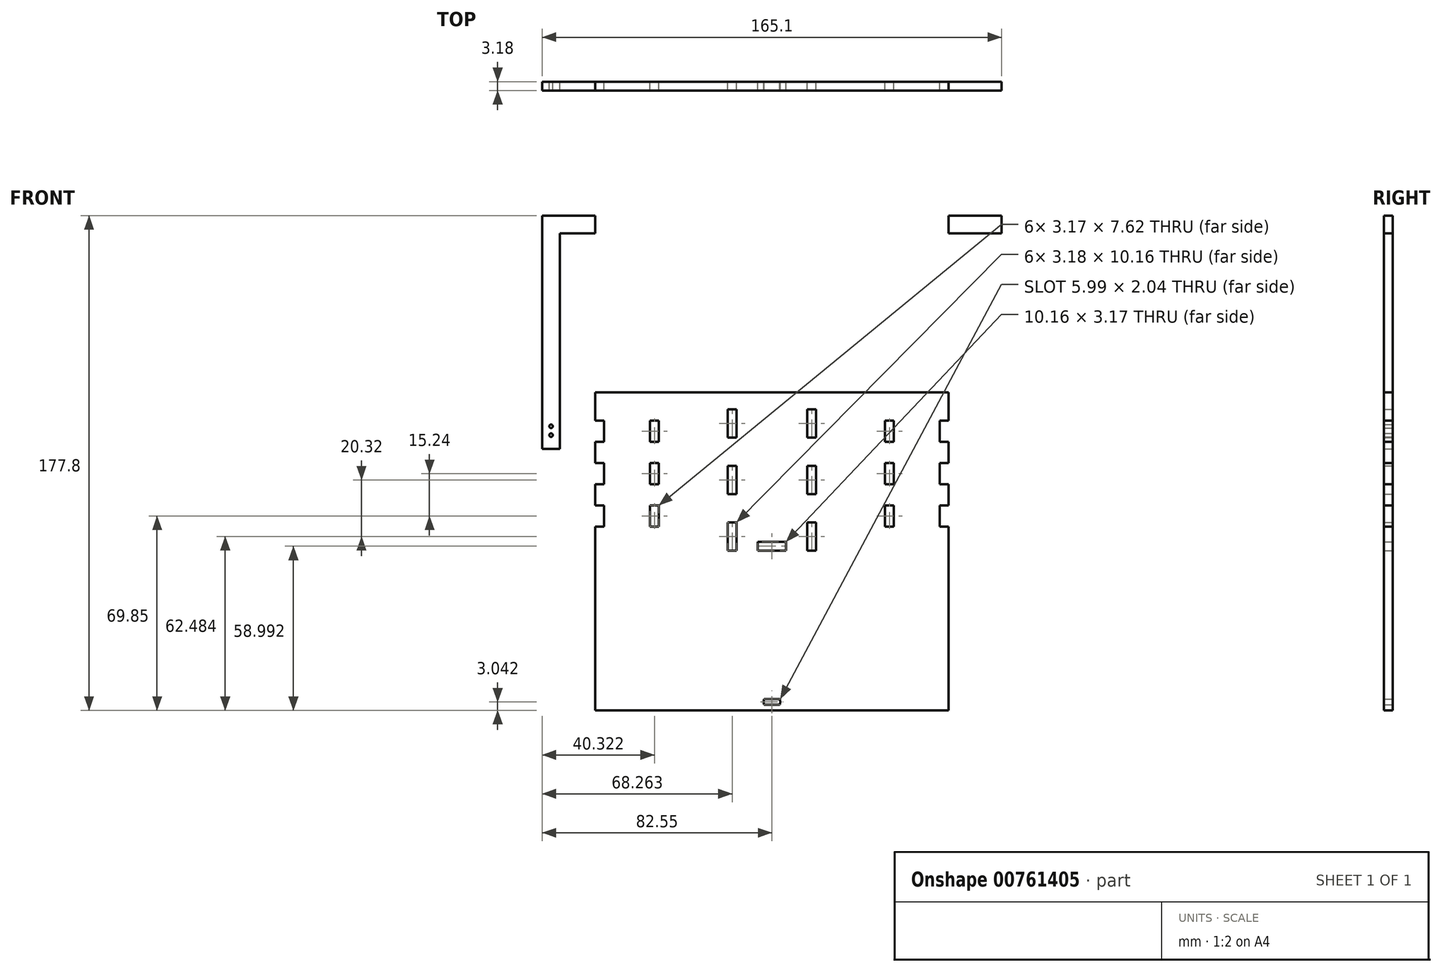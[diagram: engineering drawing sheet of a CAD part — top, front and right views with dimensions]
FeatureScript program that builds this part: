
annotation { "Feature Type Name" : "Feature", "Feature Type Description" : "" }
export const myFeature = defineFeature(function(context is Context, id is Id, definition is map)
    precondition{}
    {
        {
            var Q0;
            Q0=qCreatedBy(makeId("Front.planeOp"),FACE);
            var sketch = newSketch(context, id + "F0", { "sketchPlane" : qUnion([Q0])});
            skLineSegment(sketch, "E0.top", {"start": v(63.5, 57.15) * mm, "end": v(-63.5, 57.15) * mm});
            skPoint(sketch, "E0.middle", {"position": v(0, 0) * mm});
            skLineSegment(sketch, "E1.bottom", {"start": v(-63.5, 16.5) * mm, "end": v(-60.33, 16.5) * mm});
            skLineSegment(sketch, "E1.top", {"start": v(-63.5, 8.89) * mm, "end": v(-60.33, 8.89) * mm});
            skLineSegment(sketch, "E1.left", {"start": v(-63.5, 16.5) * mm, "end": v(-63.5, 8.89) * mm});
            skLineSegment(sketch, "E1.right", {"start": v(-60.33, 16.5) * mm, "end": v(-60.33, 8.89) * mm});
            skLineSegment(sketch, "E2.bottom", {"start": v(-43.82, 16.5) * mm, "end": v(-40.64, 16.5) * mm});
            skLineSegment(sketch, "E2.top", {"start": v(-43.82, 8.89) * mm, "end": v(-40.64, 8.89) * mm});
            skLineSegment(sketch, "E2.left", {"start": v(-43.82, 16.5) * mm, "end": v(-43.82, 8.89) * mm});
            skLineSegment(sketch, "E2.right", {"start": v(-40.64, 16.5) * mm, "end": v(-40.64, 8.89) * mm});
            skLineSegment(sketch, "E3.bottom", {"start": v(-40.64, 31.75) * mm, "end": v(-43.82, 31.75) * mm});
            skLineSegment(sketch, "E3.top", {"start": v(-40.64, 24.13) * mm, "end": v(-43.82, 24.13) * mm});
            skLineSegment(sketch, "E3.left", {"start": v(-40.64, 31.75) * mm, "end": v(-40.64, 24.13) * mm});
            skLineSegment(sketch, "E3.right", {"start": v(-43.82, 31.75) * mm, "end": v(-43.82, 24.13) * mm});
            skLineSegment(sketch, "E4.bottom", {"start": v(-60.33, 31.75) * mm, "end": v(-63.5, 31.75) * mm});
            skLineSegment(sketch, "E4.top", {"start": v(-60.33, 24.13) * mm, "end": v(-63.5, 24.13) * mm});
            skLineSegment(sketch, "E4.left", {"start": v(-60.33, 31.75) * mm, "end": v(-60.33, 24.13) * mm});
            skLineSegment(sketch, "E4.right", {"start": v(-63.5, 31.75) * mm, "end": v(-63.5, 24.13) * mm});
            skLineSegment(sketch, "E5.bottom", {"start": v(-40.64, 46.99) * mm, "end": v(-43.82, 46.99) * mm});
            skLineSegment(sketch, "E5.top", {"start": v(-40.64, 39.37) * mm, "end": v(-43.82, 39.37) * mm});
            skLineSegment(sketch, "E5.left", {"start": v(-40.64, 46.99) * mm, "end": v(-40.64, 39.37) * mm});
            skLineSegment(sketch, "E5.right", {"start": v(-43.82, 46.99) * mm, "end": v(-43.81, 39.37) * mm});
            skLineSegment(sketch, "E6.bottom", {"start": v(-60.33, 46.99) * mm, "end": v(-63.5, 46.99) * mm});
            skLineSegment(sketch, "E6.top", {"start": v(-60.33, 39.37) * mm, "end": v(-63.5, 39.37) * mm});
            skLineSegment(sketch, "E6.left", {"start": v(-60.33, 46.99) * mm, "end": v(-60.33, 39.37) * mm});
            skLineSegment(sketch, "E6.right", {"start": v(-63.5, 47) * mm, "end": v(-63.5, 39.37) * mm});
            skLineSegment(sketch, "E7.bottom", {"start": v(43.81, 31.75) * mm, "end": v(40.64, 31.75) * mm});
            skLineSegment(sketch, "E7.top", {"start": v(43.81, 24.13) * mm, "end": v(40.64, 24.13) * mm});
            skLineSegment(sketch, "E7.left", {"start": v(43.82, 31.75) * mm, "end": v(43.82, 24.13) * mm});
            skLineSegment(sketch, "E7.right", {"start": v(40.64, 31.75) * mm, "end": v(40.64, 24.13) * mm});
            skLineSegment(sketch, "E8.bottom", {"start": v(63.5, 16.5) * mm, "end": v(60.33, 16.5) * mm});
            skLineSegment(sketch, "E8.top", {"start": v(63.5, 8.89) * mm, "end": v(60.33, 8.89) * mm});
            skLineSegment(sketch, "E8.left", {"start": v(63.5, 16.5) * mm, "end": v(63.5, 8.89) * mm});
            skLineSegment(sketch, "E8.right", {"start": v(60.33, 16.5) * mm, "end": v(60.33, 8.89) * mm});
            skLineSegment(sketch, "E9.bottom", {"start": v(63.5, 46.99) * mm, "end": v(60.33, 46.99) * mm});
            skLineSegment(sketch, "E9.top", {"start": v(63.5, 39.37) * mm, "end": v(60.32, 39.37) * mm});
            skLineSegment(sketch, "E9.left", {"start": v(63.5, 46.99) * mm, "end": v(63.5, 39.37) * mm});
            skLineSegment(sketch, "E9.right", {"start": v(60.33, 46.99) * mm, "end": v(60.33, 39.37) * mm});
            skLineSegment(sketch, "E10.bottom", {"start": v(63.5, 31.75) * mm, "end": v(60.33, 31.75) * mm});
            skLineSegment(sketch, "E10.top", {"start": v(63.5, 24.13) * mm, "end": v(60.33, 24.13) * mm});
            skLineSegment(sketch, "E10.left", {"start": v(63.5, 31.75) * mm, "end": v(63.5, 24.13) * mm});
            skLineSegment(sketch, "E10.right", {"start": v(60.33, 31.75) * mm, "end": v(60.33, 24.13) * mm});
            skLineSegment(sketch, "E11.bottom", {"start": v(43.81, 16.5) * mm, "end": v(40.64, 16.5) * mm});
            skLineSegment(sketch, "E11.top", {"start": v(43.82, 8.89) * mm, "end": v(40.64, 8.89) * mm});
            skLineSegment(sketch, "E11.left", {"start": v(43.82, 16.5) * mm, "end": v(43.82, 8.89) * mm});
            skLineSegment(sketch, "E11.right", {"start": v(40.64, 16.5) * mm, "end": v(40.64, 8.89) * mm});
            skLineSegment(sketch, "E12.bottom", {"start": v(43.81, 47) * mm, "end": v(40.64, 47) * mm});
            skLineSegment(sketch, "E12.top", {"start": v(43.82, 39.37) * mm, "end": v(40.64, 39.37) * mm});
            skLineSegment(sketch, "E12.left", {"start": v(43.81, 46.99) * mm, "end": v(43.82, 39.37) * mm});
            skLineSegment(sketch, "E12.right", {"start": v(40.64, 47) * mm, "end": v(40.64, 39.37) * mm});
            skLineSegment(sketch, "E13", {"start": v(-63.5, 57.15) * mm, "end": v(-63.5, -57.15) * mm});
            skLineSegment(sketch, "E14", {"start": v(63.5, 57.15) * mm, "end": v(63.5, -57.15) * mm});
            skLineSegment(sketch, "E15.bottom", {"start": v(15.88, 0.25) * mm, "end": v(12.7, 0.25) * mm});
            skLineSegment(sketch, "E15.top", {"start": v(15.88, 10.41) * mm, "end": v(12.7, 10.41) * mm});
            skLineSegment(sketch, "E15.left", {"start": v(15.88, 0.25) * mm, "end": v(15.88, 10.41) * mm});
            skLineSegment(sketch, "E15.right", {"start": v(12.7, 0.25) * mm, "end": v(12.7, 10.41) * mm});
            skLineSegment(sketch, "E16.bottom", {"start": v(15.88, 20.57) * mm, "end": v(12.7, 20.57) * mm});
            skLineSegment(sketch, "E16.top", {"start": v(15.87, 30.73) * mm, "end": v(12.7, 30.73) * mm});
            skLineSegment(sketch, "E16.left", {"start": v(15.87, 20.57) * mm, "end": v(15.87, 30.73) * mm});
            skLineSegment(sketch, "E16.right", {"start": v(12.7, 20.57) * mm, "end": v(12.7, 30.73) * mm});
            skLineSegment(sketch, "E17.bottom", {"start": v(15.88, 40.9) * mm, "end": v(12.7, 40.9) * mm});
            skLineSegment(sketch, "E17.top", {"start": v(15.87, 51.05) * mm, "end": v(12.7, 51.05) * mm});
            skLineSegment(sketch, "E17.left", {"start": v(15.87, 40.9) * mm, "end": v(15.87, 51.05) * mm});
            skLineSegment(sketch, "E17.right", {"start": v(12.7, 40.9) * mm, "end": v(12.7, 51.05) * mm});
            skLineSegment(sketch, "E18.bottom", {"start": v(-12.7, 0.25) * mm, "end": v(-15.88, 0.25) * mm});
            skLineSegment(sketch, "E18.top", {"start": v(-12.7, 10.41) * mm, "end": v(-15.88, 10.41) * mm});
            skLineSegment(sketch, "E18.left", {"start": v(-12.7, 0.25) * mm, "end": v(-12.7, 10.41) * mm});
            skLineSegment(sketch, "E18.right", {"start": v(-15.88, 0.25) * mm, "end": v(-15.88, 10.41) * mm});
            skLineSegment(sketch, "E19.bottom", {"start": v(-12.7, 20.57) * mm, "end": v(-15.88, 20.57) * mm});
            skLineSegment(sketch, "E19.top", {"start": v(-12.7, 30.73) * mm, "end": v(-15.88, 30.73) * mm});
            skLineSegment(sketch, "E19.left", {"start": v(-12.7, 20.57) * mm, "end": v(-12.7, 30.73) * mm});
            skLineSegment(sketch, "E19.right", {"start": v(-15.88, 20.57) * mm, "end": v(-15.88, 30.73) * mm});
            skLineSegment(sketch, "E20.bottom", {"start": v(-12.7, 40.9) * mm, "end": v(-15.88, 40.9) * mm});
            skLineSegment(sketch, "E20.top", {"start": v(-12.7, 51.05) * mm, "end": v(-15.88, 51.05) * mm});
            skLineSegment(sketch, "E20.left", {"start": v(-12.7, 40.9) * mm, "end": v(-12.7, 51.05) * mm});
            skLineSegment(sketch, "E20.right", {"start": v(-15.88, 40.9) * mm, "end": v(-15.88, 51.05) * mm});
            skLineSegment(sketch, "E21.bottom", {"start": v(5.08, 0.25) * mm, "end": v(-5.08, 0.25) * mm});
            skLineSegment(sketch, "E21.top", {"start": v(5.08, 3.43) * mm, "end": v(-5.08, 3.43) * mm});
            skLineSegment(sketch, "E21.left", {"start": v(5.08, 0.25) * mm, "end": v(5.08, 3.43) * mm});
            skLineSegment(sketch, "E21.right", {"start": v(-5.08, 0.25) * mm, "end": v(-5.08, 3.43) * mm});
            skPoint(sketch, "E21.middle", {"position": v(0, 1.84) * mm});
            skLineSegment(sketch, "E22.bottom", {"start": v(-57.15, 57.15) * mm, "end": v(-63.5, 57.15) * mm});
            skLineSegment(sketch, "E22.top", {"start": v(-57.15, 120.65) * mm, "end": v(-63.5, 120.65) * mm});
            skLineSegment(sketch, "E22.left", {"start": v(-57.15, 57.15) * mm, "end": v(-57.15, 120.65) * mm});
            skLineSegment(sketch, "E22.right", {"start": v(-63.5, 57.15) * mm, "end": v(-63.5, 120.65) * mm});
            skLineSegment(sketch, "E23.bottom", {"start": v(-63.5, 120.65) * mm, "end": v(-82.55, 120.65) * mm});
            skLineSegment(sketch, "E23.top", {"start": v(-63.5, 114.3) * mm, "end": v(-82.55, 114.3) * mm});
            skLineSegment(sketch, "E23.left", {"start": v(-63.5, 120.65) * mm, "end": v(-63.5, 114.3) * mm});
            skLineSegment(sketch, "E23.right", {"start": v(-82.55, 120.65) * mm, "end": v(-82.55, 114.3) * mm});
            skLineSegment(sketch, "E24.bottom", {"start": v(-82.55, 120.65) * mm, "end": v(-76.2, 120.65) * mm});
            skLineSegment(sketch, "E24.top", {"start": v(-82.55, 36.83) * mm, "end": v(-76.2, 36.83) * mm});
            skLineSegment(sketch, "E24.left", {"start": v(-82.55, 120.65) * mm, "end": v(-82.55, 36.83) * mm});
            skLineSegment(sketch, "E24.right", {"start": v(-76.2, 120.65) * mm, "end": v(-76.2, 36.83) * mm});
            skLineSegment(sketch, "E25.bottom", {"start": v(63.5, 57.15) * mm, "end": v(57.15, 57.15) * mm});
            skLineSegment(sketch, "E25.top", {"start": v(63.5, 120.65) * mm, "end": v(57.15, 120.65) * mm});
            skLineSegment(sketch, "E25.left", {"start": v(63.5, 57.15) * mm, "end": v(63.5, 120.65) * mm});
            skLineSegment(sketch, "E25.right", {"start": v(57.15, 57.15) * mm, "end": v(57.15, 120.65) * mm});
            skLineSegment(sketch, "E26.bottom", {"start": v(63.5, 120.65) * mm, "end": v(82.55, 120.65) * mm});
            skLineSegment(sketch, "E26.top", {"start": v(63.5, 114.3) * mm, "end": v(82.55, 114.3) * mm});
            skLineSegment(sketch, "E26.left", {"start": v(63.5, 120.65) * mm, "end": v(63.5, 114.3) * mm});
            skLineSegment(sketch, "E26.right", {"start": v(82.55, 120.65) * mm, "end": v(82.55, 114.3) * mm});
            skLineSegment(sketch, "E27.bottom", {"start": v(82.55, 114.3) * mm, "end": v(76.2, 114.3) * mm});
            skLineSegment(sketch, "E27.top", {"start": v(82.55, 36.83) * mm, "end": v(76.2, 36.83) * mm});
            skLineSegment(sketch, "E27.left", {"start": v(82.55, 114.3) * mm, "end": v(82.55, 36.83) * mm});
            skLineSegment(sketch, "E27.right", {"start": v(76.2, 114.3) * mm, "end": v(76.2, 36.83) * mm});
            skCircle(sketch, "E28", {"center": v(-79.38, 41.77) * mm, "radius": 0.64 * mm});
            skPoint(sketch, "E28.centerSnap0", {"position": v(-79.38, 36.83) * mm});
            skCircle(sketch, "E29", {"center": v(-79.38, 44.95) * mm, "radius": 0.64 * mm});
            skCircle(sketch, "E30", {"center": v(79.38, 41.77) * mm, "radius": 0.64 * mm});
            skCircle(sketch, "E31", {"center": v(79.38, 44.95) * mm, "radius": 0.64 * mm});
            skPoint(sketch, "E32", {"position": v(79.38, 36.83) * mm});
            skLineSegment(sketch, "E33", {"start": v(-63.5, -57.15) * mm, "end": v(63.5, -57.15) * mm});
            skLineSegment(sketch, "E34.bottom", {"start": v(2.82, -55.13) * mm, "end": v(-2.82, -55.13) * mm});
            skLineSegment(sketch, "E34.top", {"start": v(2.82, -53.09) * mm, "end": v(-2.82, -53.09) * mm});
            skPoint(sketch, "E34.middle", {"position": v(0, -54.1) * mm});
            skArc(sketch, "E35", {"start": v(-2.82, -53.09) * mm, "mid": v(-3, -54.1) * mm, "end": v(-2.82, -55.13) * mm});
            skArc(sketch, "E36.trimOffspring", {"start": v(2.82, -55.13) * mm, "mid": v(3, -54.1) * mm, "end": v(2.82, -53.09) * mm});
            skSolve(sketch);
        }
        {
            var Q0;
            {var subQ13=sQuery(id+"F0.wireOp",EDGE,"E0.bottom");Q0=makeQuery(id+"F0.imprint","IMPRINT",FACE,{"disambiguationData":[TD([[makeQuery(id+"F0.imprint","IMPRINT",EDGE,{"derivedFrom":subQ13}),-1.0]])]});}
            var Q1;
            Q1=makeQuery(id+"F0.imprint","IMPRINT",FACE,{"disambiguationData":[TD([[makeQuery(id+"F0.imprint","IMPRINT",EDGE,{"derivedFrom":sQuery(id+"F0.wireOp",EDGE,"E22.bottom")}),-1.0]])]});
            var Q2;
            {var subQ0=sQuery(id+"F0.wireOp",EDGE,"E23.bottom");Q2=makeQuery(id+"F0.imprint","IMPRINT",FACE,{"disambiguationData":[TD([[makeQuery(id+"F0.imprint","IMPRINT",EDGE,{"derivedFrom":subQ0}),1.0]])]});}
            var Q3;
            {var subQ5=sQuery(id+"F0.wireOp",EDGE,"E24.bottom");Q3=makeQuery(id+"F0.imprint","IMPRINT",FACE,{"disambiguationData":[TD([[makeQuery(id+"F0.imprint","IMPRINT",EDGE,{"derivedFrom":subQ5}),-1.0]])]});}
            var Q4;
            {var subQ5=sQuery(id+"F0.wireOp",EDGE,"E24.top");Q4=makeQuery(id+"F0.imprint","IMPRINT",FACE,{"disambiguationData":[TD([[makeQuery(id+"F0.imprint","IMPRINT",EDGE,{"derivedFrom":subQ5}),1.0]])]});}
            var Q5;
            Q5=makeQuery(id+"F0.imprint","IMPRINT",FACE,{"disambiguationData":[TD([[makeQuery(id+"F0.imprint","IMPRINT",EDGE,{"derivedFrom":sQuery(id+"F0.wireOp",EDGE,"E25.bottom")}),-1.0]])]});
            var Q6;
            Q6=makeQuery(id+"F0.imprint","IMPRINT",FACE,{"disambiguationData":[TD([[makeQuery(id+"F0.imprint","IMPRINT",EDGE,{"derivedFrom":sQuery(id+"F0.wireOp",EDGE,"E26.bottom")}),-1.0]])]});
            var Q7;
            Q7=makeQuery(id+"F0.imprint","IMPRINT",FACE,{"disambiguationData":[TD([[makeQuery(id+"F0.imprint","IMPRINT",EDGE,{"derivedFrom":sQuery(id+"F0.wireOp",EDGE,"E27.bottom")}),1.0]])]});
            var Q8;
            Q8=makeQuery(id+"F0.imprint","IMPRINT",FACE,{"disambiguationData":[TD([[makeQuery(id+"F0.imprint","IMPRINT",EDGE,{"derivedFrom":sQuery(id+"F0.wireOp",EDGE,"E0.top")}),1.0]])]});
            extrude(context, id + "F1", {"entities" : qUnion([Q0, Q1, Q2, Q3, Q4, Q5, Q6, Q7, Q8]), "depth" : 3.17 * mm, "offsetDistance" : 25.4 * mm});
        }
    });
